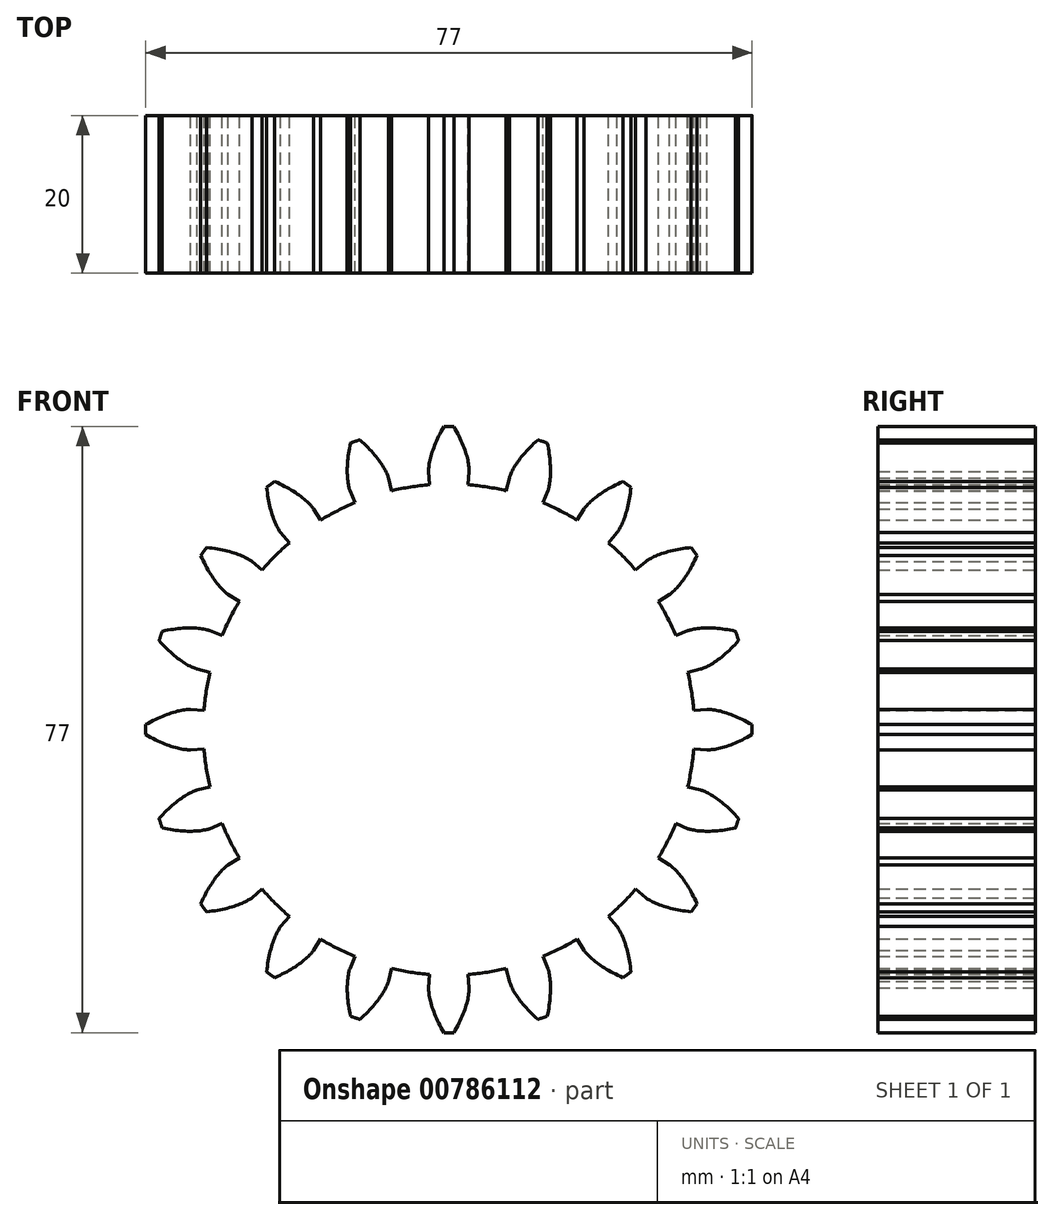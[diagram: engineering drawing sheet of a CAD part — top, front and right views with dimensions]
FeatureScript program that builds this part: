
annotation { "Feature Type Name" : "Feature", "Feature Type Description" : "" }
export const myFeature = defineFeature(function(context is Context, id is Id, definition is map)
    precondition{}
    {
        {
            var Q0;
            Q0=qCreatedBy(makeId("Front.planeOp"),FACE);
            var sketch = newSketch(context, id + "F0", { "sketchPlane" : qUnion([Q0])});
            skCircle(sketch, "E0", {"center": v(-100, 0) * mm, "radius": 35 * mm});
            skCircle(sketch, "E1.0", {"center": v(-100, 0) * mm, "radius": 38.5 * mm});
            skCircle(sketch, "E2.0", {"center": v(-100, 0) * mm, "radius": 31.2 * mm});
            skLineSegment(sketch, "E3", {"start": v(-123.7, 35) * mm, "end": v(-72.95, 35) * mm, "construction": true});
            skLineSegment(sketch, "E4", {"start": v(-100, 35) * mm, "end": v(-107.56, 37.75) * mm});
            skLineSegment(sketch, "E5", {"start": v(-100, 35) * mm, "end": v(-88.75, 30.9) * mm});
            skArc(sketch, "E6", {"start": v(-88.75, 30.9) * mm, "mid": v(-98.53, 32.86) * mm, "end": v(-108.45, 31.79) * mm});
            skLineSegment(sketch, "E7", {"start": v(-88.75, 30.9) * mm, "end": v(-100, 0) * mm});
            skLineSegment(sketch, "E8", {"start": v(-108.45, 31.79) * mm, "end": v(-100, 0) * mm});
            skLineSegment(sketch, "E9", {"start": v(-92.59, 32.04) * mm, "end": v(-100, 0) * mm});
            skLineSegment(sketch, "E10", {"start": v(-96.54, 32.7) * mm, "end": v(-100, 0) * mm});
            skLineSegment(sketch, "E11", {"start": v(-100.53, 32.88) * mm, "end": v(-100, 0) * mm});
            skLineSegment(sketch, "E12", {"start": v(-104.52, 32.58) * mm, "end": v(-100, 0) * mm});
            skLineSegment(sketch, "E13", {"start": v(-92.59, 32.04) * mm, "end": v(-108.19, 35.65) * mm});
            skLineSegment(sketch, "E14", {"start": v(-108.48, 33.97) * mm, "end": v(-96.54, 32.7) * mm});
            skLineSegment(sketch, "E15", {"start": v(-108.54, 32.75) * mm, "end": v(-100.53, 32.88) * mm});
            skLineSegment(sketch, "E16", {"start": v(-108.49, 32.03) * mm, "end": v(-104.52, 32.58) * mm});
            skFitSpline(sketch, "E17", {"points": [v(-108.45, 31.79) * mm, v(-108.49, 32.03) * mm, v(-108.54, 32.75) * mm, v(-108.48, 33.97) * mm, v(-108.19, 35.65) * mm, v(-107.56, 37.75) * mm], "startDerivative": vector(-0.44, 2.22) * mm, "endDerivative": vector(2.47, 7.56) * mm});
            skCircle(sketch, "E18", {"center": v(100, 0) * mm, "radius": 35 * mm});
            skCircle(sketch, "E19.0", {"center": v(100, 0) * mm, "radius": 38.5 * mm});
            skCircle(sketch, "E20.0", {"center": v(100, 0) * mm, "radius": 31.2 * mm});
            skArc(sketch, "E21", {"start": v(116.63, 28.37) * mm, "mid": v(107.37, 32.05) * mm, "end": v(97.42, 32.79) * mm});
            skLineSegment(sketch, "E22", {"start": v(116.63, 28.37) * mm, "end": v(100, 0) * mm});
            skLineSegment(sketch, "E23", {"start": v(97.42, 32.79) * mm, "end": v(100, 0) * mm});
            skLineSegment(sketch, "E24", {"start": v(113.07, 30.18) * mm, "end": v(100, 0) * mm});
            skLineSegment(sketch, "E25", {"start": v(109.3, 31.55) * mm, "end": v(100, 0) * mm});
            skLineSegment(sketch, "E26", {"start": v(105.4, 32.44) * mm, "end": v(100, 0) * mm});
            skLineSegment(sketch, "E27", {"start": v(101.42, 32.86) * mm, "end": v(100, 0) * mm});
            skLineSegment(sketch, "E28", {"start": v(113.07, 30.18) * mm, "end": v(98.37, 36.54) * mm});
            skLineSegment(sketch, "E29", {"start": v(97.78, 34.94) * mm, "end": v(109.3, 31.55) * mm});
            skLineSegment(sketch, "E30", {"start": v(97.5, 33.76) * mm, "end": v(105.4, 32.44) * mm});
            skLineSegment(sketch, "E31", {"start": v(97.42, 33.03) * mm, "end": v(101.42, 32.86) * mm});
            skFitSpline(sketch, "E32", {"points": [v(97.42, 32.79) * mm, v(97.42, 33.03) * mm, v(97.5, 33.76) * mm, v(97.78, 34.94) * mm, v(98.37, 36.54) * mm, v(99.37, 38.5) * mm], "startDerivative": vector(-0.44, 2.22) * mm, "endDerivative": vector(2.47, 7.56) * mm});
            skLineSegment(sketch, "E33", {"start": v(100, 0) * mm, "end": v(100, 42.16) * mm, "construction": true});
            skArc(sketch, "E34.0", {"start": v(0.63, 38.5) * mm, "mid": v(0, 38.5) * mm, "end": v(-0.63, 38.5) * mm});
            skArc(sketch, "E35.0", {"start": v(2.45, 31.1) * mm, "mid": v(0, 31.2) * mm, "end": v(-2.45, 31.1) * mm});
            skLineSegment(sketch, "E36", {"start": v(-2.58, 32.79) * mm, "end": v(-2.45, 31.1) * mm});
            skFitSpline(sketch, "E37", {"points": [v(-2.58, 32.79) * mm, v(-2.58, 33.03) * mm, v(-2.5, 33.76) * mm, v(-2.22, 34.94) * mm, v(-1.63, 36.54) * mm, v(-0.63, 38.5) * mm], "startDerivative": vector(-0.44, 2.22) * mm, "endDerivative": vector(4.14, 7.3) * mm});
            skLineSegment(sketch, "E38", {"start": v(0, 0) * mm, "end": v(0, 42.16) * mm, "construction": true});
            skFitSpline(sketch, "E39.MirrorCS", {"points": [v(2.58, 32.79) * mm, v(2.58, 33.03) * mm, v(2.5, 33.76) * mm, v(2.22, 34.94) * mm, v(1.63, 36.54) * mm, v(0.63, 38.5) * mm], "startDerivative": vector(0.44, 2.22) * mm, "endDerivative": vector(-4.14, 7.3) * mm});
            skLineSegment(sketch, "E40.MirrorCS", {"start": v(2.58, 32.79) * mm, "end": v(2.45, 31.1) * mm});
            skSolve(sketch);
        }
        {
            var Q0;
            Q0=makeQuery(id+"F0.imprint","IMPRINT",FACE,{"disambiguationData":[TD([[makeQuery(id+"F0.imprint","IMPRINT",EDGE,{"derivedFrom":sQuery(id+"F0.wireOp",EDGE,"E34.0")}),1.0]])]});
            extrude(context, id + "F1", {"entities" : qUnion([Q0]), "depth" : 20 * mm, "offsetDistance" : 25 * mm});
        }
        {
            var Q0;
            Q0=qCreatedBy(makeId("Top.planeOp"),FACE);
            var sketch = newSketch(context, id + "F2", { "sketchPlane" : qUnion([Q0])});
            skLineSegment(sketch, "E41", {"start": v(0, 27.53) * mm, "end": v(0, -36.15) * mm, "construction": true});
            skSolve(sketch);
        }
        {
            var Q0;
            Q0=makeQuery(id+"F1.opExtrude","SWEPT_BODY",BODY,{"disambiguationData":[OSD([sQuery(id+"F0.wireOp",EDGE,"E34.0"),sQuery(id+"F0.wireOp",EDGE,"E35.0"),sQuery(id+"F0.wireOp",EDGE,"E36"),sQuery(id+"F0.wireOp",EDGE,"E37"),sQuery(id+"F0.wireOp",EDGE,"E39.MirrorCS"),sQuery(id+"F0.wireOp",EDGE,"E40.MirrorCS")])]});
            var Q1;
            Q1=sQuery(id+"F2.wireOp",EDGE,"E41");
            circularPattern(context, id + "F3", {"entities" : qUnion([Q0]), "axis" : qUnion([Q1]), "angle" : 360 * degree, "instanceCount" : 20, "equalSpace" : true});
        }
        {
            var Q0;
            Q0=qCreatedBy(makeId("Front.planeOp"),FACE);
            var sketch = newSketch(context, id + "F4", { "sketchPlane" : qUnion([Q0])});
            skCircle(sketch, "E42", {"center": v(0, 0) * mm, "radius": 31.2 * mm});
            skPoint(sketch, "E43.0", {"position": v(2.45, 31.1) * mm});
            skSolve(sketch);
        }
        {
            var Q0;
            Q0=makeQuery(id+"F4.imprint","IMPRINT",FACE,{"disambiguationData":[TD([[makeQuery(id+"F4.imprint","IMPRINT",EDGE,{"derivedFrom":sQuery(id+"F4.wireOp",EDGE,"E42")}),1.0]])]});
            extrude(context, id + "F5", {"entities" : qUnion([Q0]), "operationType" : NewBodyOperationType.ADD, "depth" : 20 * mm, "offsetDistance" : 25 * mm});
        }
    });
